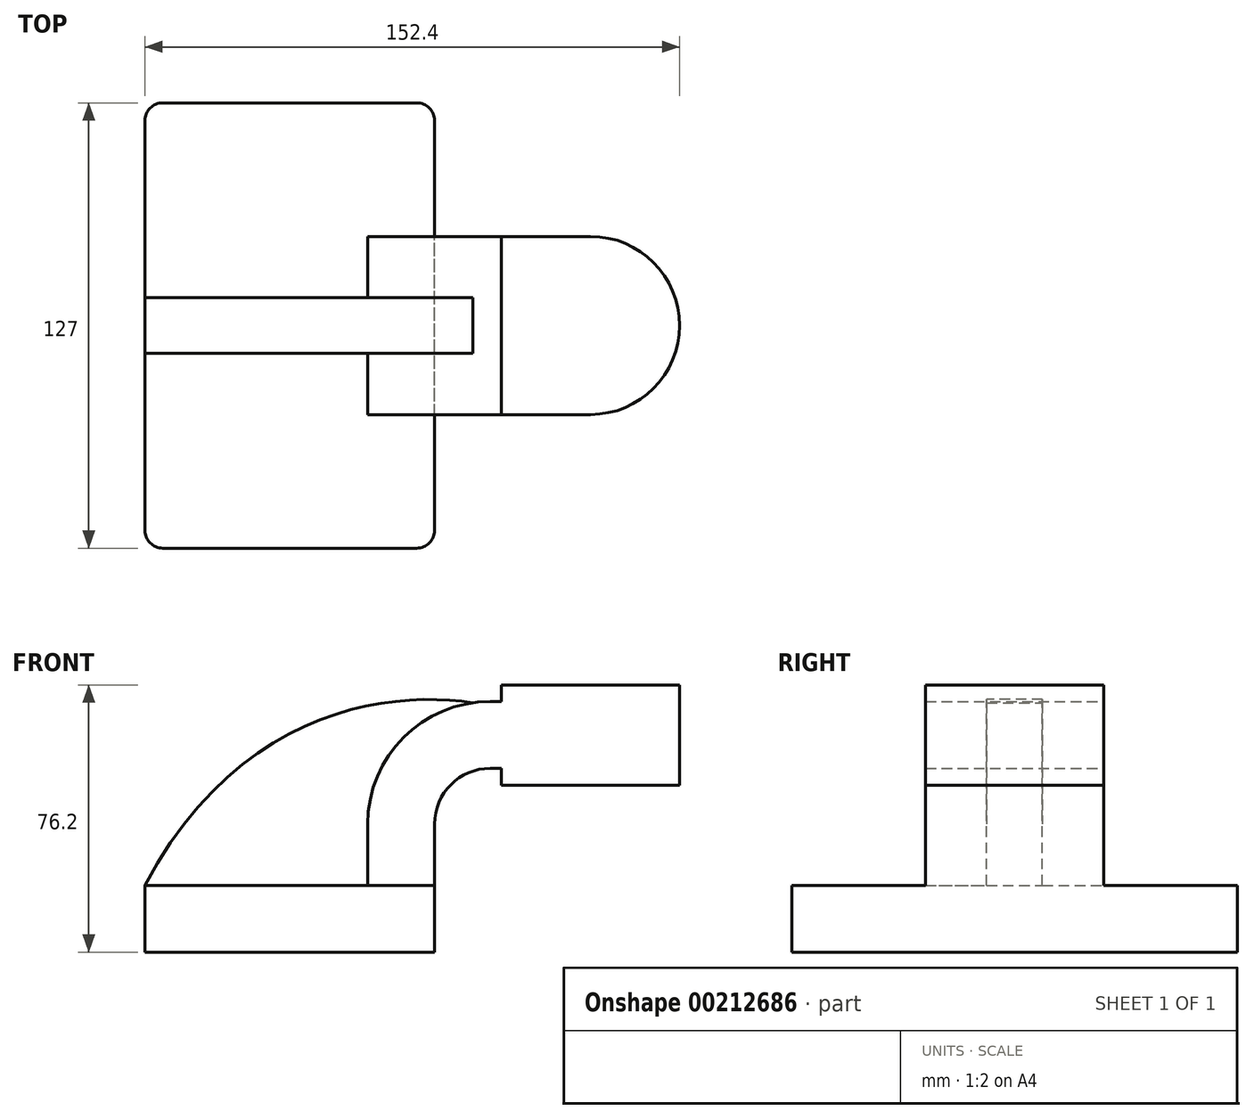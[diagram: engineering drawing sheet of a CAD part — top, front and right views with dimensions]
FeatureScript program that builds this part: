
annotation { "Feature Type Name" : "Feature", "Feature Type Description" : "" }
export const myFeature = defineFeature(function(context is Context, id is Id, definition is map)
    precondition{}
    {
        {
            var Q0;
            Q0=qCreatedBy(makeId("Front.planeOp"),FACE);
            var sketch = newSketch(context, id + "F0", { "sketchPlane" : qUnion([Q0])});
            skLineSegment(sketch, "E0.bottom", {"start": v(-41.28, 9.52) * mm, "end": v(41.28, 9.53) * mm});
            skLineSegment(sketch, "E0.top", {"start": v(-41.28, -9.53) * mm, "end": v(41.28, -9.53) * mm});
            skLineSegment(sketch, "E0.left", {"start": v(-41.28, 9.52) * mm, "end": v(-41.28, -9.53) * mm});
            skLineSegment(sketch, "E0.right", {"start": v(41.28, 9.53) * mm, "end": v(41.28, -9.52) * mm});
            skPoint(sketch, "E0.middle", {"position": v(0, 0) * mm});
            skLineSegment(sketch, "E1.bottom", {"start": v(111.12, 66.67) * mm, "end": v(60.32, 66.67) * mm});
            skLineSegment(sketch, "E1.top", {"start": v(111.12, 38.1) * mm, "end": v(60.33, 38.1) * mm});
            skLineSegment(sketch, "E1.left", {"start": v(111.12, 66.68) * mm, "end": v(111.12, 38.1) * mm});
            skLineSegment(sketch, "E1.right", {"start": v(60.32, 66.68) * mm, "end": v(60.33, 38.1) * mm});
            skPoint(sketch, "E1.middle", {"position": v(85.72, 52.39) * mm});
            skLineSegment(sketch, "E2", {"start": v(41.27, 9.53) * mm, "end": v(41.27, 27) * mm});
            skArc(sketch, "E3", {"start": v(41.27, 27) * mm, "mid": v(45.92, 38.23) * mm, "end": v(57.15, 42.88) * mm});
            skLineSegment(sketch, "E4", {"start": v(57.15, 42.88) * mm, "end": v(85.72, 42.88) * mm});
            skLineSegment(sketch, "E5.0", {"start": v(57.15, 61.93) * mm, "end": v(85.72, 61.93) * mm});
            skArc(sketch, "E5.1", {"start": v(22.22, 27) * mm, "mid": v(32.45, 51.7) * mm, "end": v(57.15, 61.93) * mm});
            skLineSegment(sketch, "E5.2", {"start": v(22.22, 9.53) * mm, "end": v(22.22, 27) * mm});
            skFitSpline(sketch, "E6", {"points": [v(-41.28, 9.52) * mm, v(52.23, 61.58) * mm], "startDerivative": vector(79.51, 150.76) * mm, "endDerivative": vector(72.2, -11.22) * mm});
            skLineSegment(sketch, "E7", {"start": v(85.72, 38.1) * mm, "end": v(85.72, 66.67) * mm});
            skSolve(sketch);
        }
        {
            var Q0;
            Q0=makeQuery(id+"F0.imprint","IMPRINT",FACE,{"disambiguationData":[TD([[makeQuery(id+"F0.imprint","IMPRINT",EDGE,{"derivedFrom":sQuery(id+"F0.wireOp",EDGE,"E0.top")}),1.0]])]});
            extrude(context, id + "F1", {"entities" : qUnion([Q0]), "endBound" : BoundingType.SYMMETRIC, "depth" : 127 * mm});
        }
        {
            var Q0;
            {var subQ5=sQuery(id+"F0.wireOp",EDGE,"E2");Q0=makeQuery(id+"F0.imprint","IMPRINT",FACE,{"disambiguationData":[TD([[makeQuery(id+"F0.imprint","IMPRINT",EDGE,{"derivedFrom":subQ5}),1.0]])]});}
            var Q1;
            {var subQ0=sQuery(id+"F0.wireOp",EDGE,"E5.0");var subQ1=sQuery(id+"F0.wireOp",EDGE,"E1.right");var subQ2=makeQuery(id+"F0.imprint","INTERSECT",VERTEX,{"derivedFrom":[subQ1,subQ0]});Q1=makeQuery(id+"F0.imprint","IMPRINT",FACE,{"disambiguationData":[TD([[makeQuery(id+"F0.imprint","IMPRINT",EDGE,{"disambiguationData":[TD([[subQ2,-1.0]])],"derivedFrom":subQ1}),1.0]])]});}
            var Q2;
            {var subQ0=sQuery(id+"F0.wireOp",EDGE,"E1.right");var subQ1=sQuery(id+"F0.wireOp",EDGE,"E1.bottom");var subQ2=makeQuery(id+"F0.imprint","INTERSECT",VERTEX,{"derivedFrom":[subQ1,subQ0]});Q2=makeQuery(id+"F0.imprint","IMPRINT",FACE,{"disambiguationData":[TD([[makeQuery(id+"F0.imprint","IMPRINT",EDGE,{"disambiguationData":[TD([[subQ2,1.0]])],"derivedFrom":subQ1}),1.0]])]});}
            var Q3;
            {var subQ0=sQuery(id+"F0.wireOp",EDGE,"E1.right");var subQ1=sQuery(id+"F0.wireOp",EDGE,"E1.top");var subQ2=makeQuery(id+"F0.imprint","INTERSECT",VERTEX,{"derivedFrom":[subQ1,subQ0]});Q3=makeQuery(id+"F0.imprint","IMPRINT",FACE,{"disambiguationData":[TD([[makeQuery(id+"F0.imprint","IMPRINT",EDGE,{"disambiguationData":[TD([[subQ2,1.0]])],"derivedFrom":subQ1}),-1.0]])]});}
            extrude(context, id + "F2", {"entities" : qUnion([Q0, Q1, Q2, Q3]), "operationType" : NewBodyOperationType.ADD, "endBound" : BoundingType.SYMMETRIC, "depth" : 50.8 * mm});
        }
        {
            var Q0;
            {var subQ2=sQuery(id+"F0.wireOp",EDGE,"E5.2");Q0=makeQuery(id+"F0.imprint","IMPRINT",FACE,{"disambiguationData":[TD([[makeQuery(id+"F0.imprint","IMPRINT",EDGE,{"derivedFrom":subQ2}),1.0]])]});}
            extrude(context, id + "F3", {"entities" : qUnion([Q0]), "operationType" : NewBodyOperationType.ADD, "endBound" : BoundingType.SYMMETRIC, "depth" : 15.88 * mm});
        }
        {
            var Q0;
            {var subQ4=sQuery(id+"F0.wireOp",EDGE,"E1.left");Q0=makeQuery(id+"F0.imprint","IMPRINT",FACE,{"disambiguationData":[TD([[makeQuery(id+"F0.imprint","IMPRINT",EDGE,{"derivedFrom":subQ4}),-1.0]])]});}
            var Q1;
            Q1=sQuery(id+"F0.wireOp",EDGE,"E7");
            revolve(context, id + "F4", {"operationType" : NewBodyOperationType.ADD, "entities" : qUnion([Q0]), "axis" : qUnion([Q1]), "revolveType" : RevolveType.FULL});
        }
        {
            var Q0;
            Q0=makeQuery(id+"F1.opExtrude","CAP_EDGE",EDGE,{"disambiguationData":[OSD([sQuery(id+"F0.wireOp",EDGE,"E0.right")])],"isStart":true});
            var Q1;
            Q1=makeQuery(id+"F1.opExtrude","CAP_EDGE",EDGE,{"disambiguationData":[OSD([sQuery(id+"F0.wireOp",EDGE,"E0.right")])],"isStart":false});
            var Q2;
            Q2=makeQuery(id+"F1.opExtrude","CAP_EDGE",EDGE,{"disambiguationData":[OSD([sQuery(id+"F0.wireOp",EDGE,"E0.left")])],"isStart":false});
            var Q3;
            Q3=makeQuery(id+"F1.opExtrude","CAP_EDGE",EDGE,{"disambiguationData":[OSD([sQuery(id+"F0.wireOp",EDGE,"E0.left")])],"isStart":true});
            fillet(context, id + "F5", {"entities" : qUnion([Q0, Q1, Q2, Q3]), "radius" : 5.08 * mm, "tangentPropagation" : true, "allowEdgeOverflow" : false});
        }
    });
